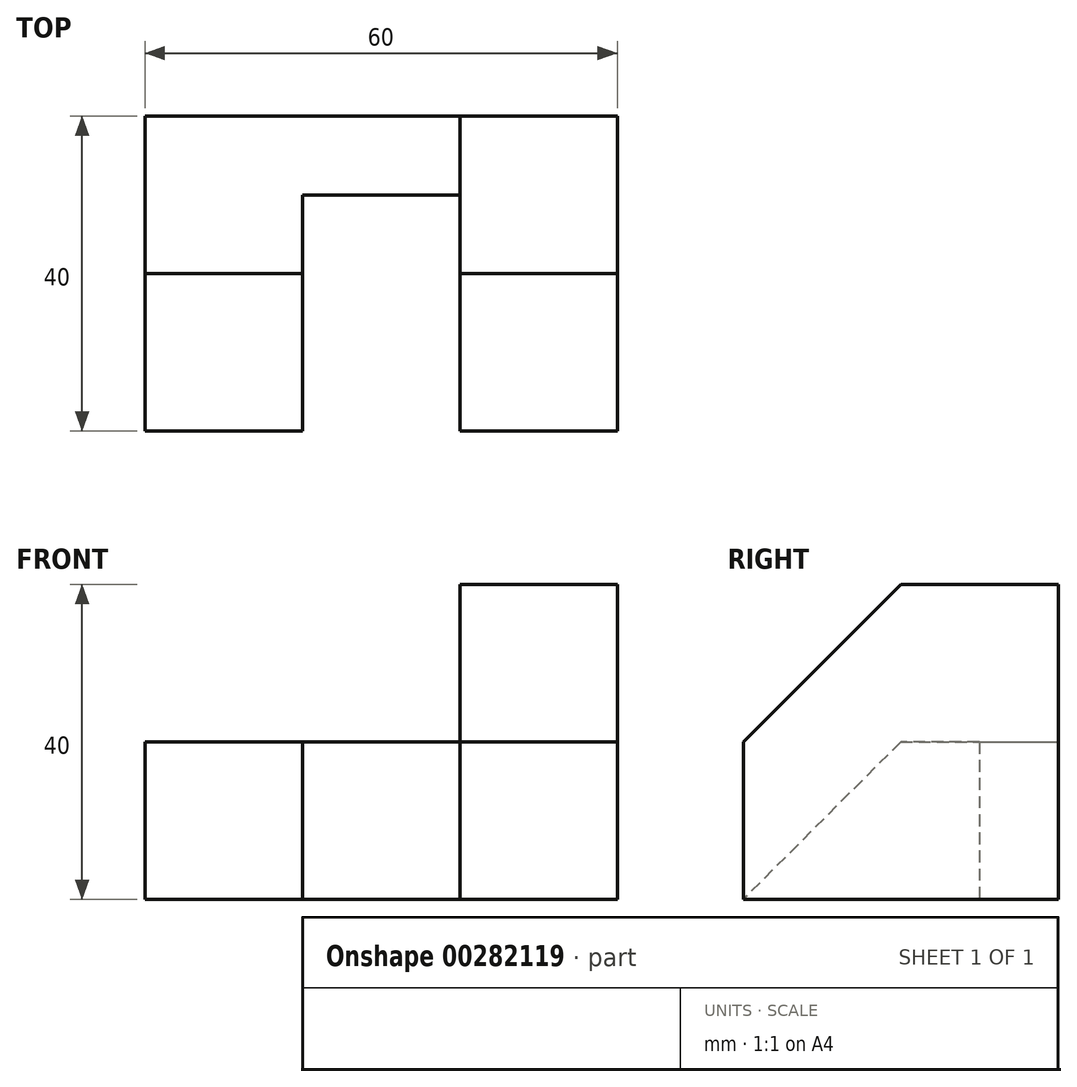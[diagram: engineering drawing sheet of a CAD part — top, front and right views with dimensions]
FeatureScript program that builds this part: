
annotation { "Feature Type Name" : "Feature", "Feature Type Description" : "" }
export const myFeature = defineFeature(function(context is Context, id is Id, definition is map)
    precondition{}
    {
        {
            var Q0;
            Q0=qCreatedBy(makeId("Right.planeOp"),FACE);
            var sketch = newSketch(context, id + "F0", { "sketchPlane" : qUnion([Q0])});
            skLineSegment(sketch, "E0", {"start": v(36.24, 0) * mm, "end": v(-3.76, 0) * mm});
            skLineSegment(sketch, "E1", {"start": v(-3.76, 0) * mm, "end": v(-3.76, 20) * mm});
            skLineSegment(sketch, "E2", {"start": v(-3.76, 20) * mm, "end": v(16.24, 40) * mm});
            skLineSegment(sketch, "E3", {"start": v(36.24, 0) * mm, "end": v(36.24, 40) * mm});
            skLineSegment(sketch, "E4", {"start": v(36.24, 40) * mm, "end": v(16.24, 40) * mm});
            skSolve(sketch);
        }
        {
            var Q0;
            Q0 = qSketchRegion(id + "F0", true);
            extrude(context, id + "F1", {"entities" : qUnion([Q0]), "oppositeDirection" : true, "depth" : 20 * mm});
        }
        {
            var Q0;
            Q0=makeQuery(id+"F1.opExtrude","CAP_FACE",FACE,{"disambiguationData":[OSD([sQuery(id+"F0.wireOp",EDGE,"E0"),sQuery(id+"F0.wireOp",EDGE,"E1"),sQuery(id+"F0.wireOp",EDGE,"E2"),sQuery(id+"F0.wireOp",EDGE,"E3"),sQuery(id+"F0.wireOp",EDGE,"E4")])],"isStart":false});
            var sketch = newSketch(context, id + "F2", { "sketchPlane" : qUnion([Q0])});
            skLineSegment(sketch, "E5", {"start": v(3.76, 20) * mm, "end": v(-36.24, 20) * mm});
            skSolve(sketch);
        }
        {
            var Q0;
            Q0 = qSketchRegion(id + "F2", true);
            var Q1;
            {var subQ0=sQuery(id+"F2.wireOp",EDGE,"E5");Q1=makeQuery(id+"F2.imprint","IMPRINT",FACE,{"disambiguationData":[TD([[makeQuery(id+"F2.imprint","IMPRINT",EDGE,{"derivedFrom":subQ0}),1.0]])]});}
            extrude(context, id + "F3", {"entities" : qUnion([Q0, Q1]), "operationType" : NewBodyOperationType.ADD, "depth" : 40 * mm});
        }
        {
            var Q0;
            Q0=makeQuery(id+"F3.opExtrude","CAP_FACE",FACE,{"disambiguationData":[OSD([sQuery(id+"F0.wireOp",EDGE,"E0"),sQuery(id+"F0.wireOp",EDGE,"E1"),sQuery(id+"F0.wireOp",EDGE,"E3"),sQuery(id+"F2.wireOp",EDGE,"E5")])],"isStart":false});
            var sketch = newSketch(context, id + "F4", { "sketchPlane" : qUnion([Q0])});
            skLineSegment(sketch, "E6", {"start": v(-16.24, 20) * mm, "end": v(3.76, 0) * mm});
            skSolve(sketch);
        }
        {
            var Q0;
            Q0 = qSketchRegion(id + "F4", true);
            var Q1;
            {var subQ0=sQuery(id+"F4.wireOp",EDGE,"E6");Q1=makeQuery(id+"F4.imprint","IMPRINT",FACE,{"disambiguationData":[TD([[makeQuery(id+"F4.imprint","IMPRINT",EDGE,{"derivedFrom":subQ0}),1.0]])]});}
            extrude(context, id + "F5", {"entities" : qUnion([Q0, Q1]), "operationType" : NewBodyOperationType.REMOVE, "oppositeDirection" : true, "depth" : 40 * mm});
        }
        {
            var Q0;
            {var subQ0=sQuery(id+"F0.wireOp",EDGE,"E0");Q0=makeQuery(id+"F3.boolean.opBoolean","MERGE",FACE,{"derivedFrom":[makeQuery(id+"F1.opExtrude","SWEPT_FACE",FACE,{"disambiguationData":[OSD([subQ0])]}),makeQuery(id+"F3.opExtrude","SWEPT_FACE",FACE,{"disambiguationData":[OSD([subQ0])]})]});}
            var sketch = newSketch(context, id + "F6", { "sketchPlane" : qUnion([Q0])});
            skLineSegment(sketch, "E7", {"start": v(-20, 3.76) * mm, "end": v(-20, -26.24) * mm});
            skLineSegment(sketch, "E8", {"start": v(-20, -26.24) * mm, "end": v(-40, -26.24) * mm});
            skLineSegment(sketch, "E9", {"start": v(-40, -26.24) * mm, "end": v(-40, 3.76) * mm});
            skLineSegment(sketch, "E10", {"start": v(-40, 3.76) * mm, "end": v(-20, 3.76) * mm});
            skSolve(sketch);
        }
        {
            var Q0;
            Q0 = qSketchRegion(id + "F6", true);
            extrude(context, id + "F7", {"entities" : qUnion([Q0]), "operationType" : NewBodyOperationType.REMOVE, "oppositeDirection" : true, "depth" : 25 * mm});
        }
    });
